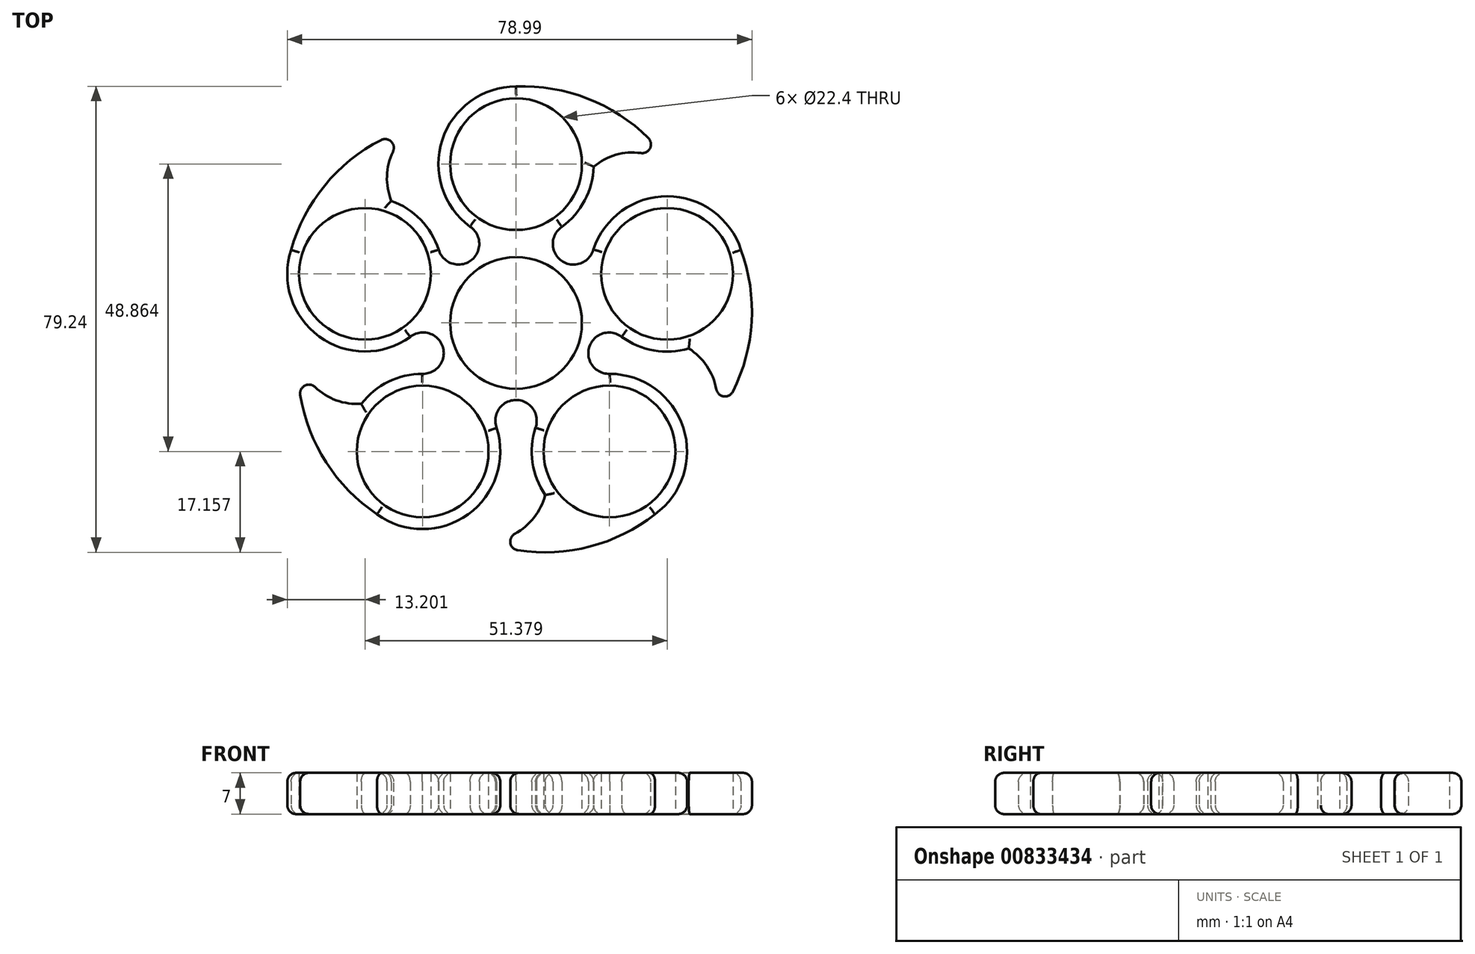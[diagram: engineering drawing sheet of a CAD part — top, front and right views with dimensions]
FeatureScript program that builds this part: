
annotation { "Feature Type Name" : "Feature", "Feature Type Description" : "" }
export const myFeature = defineFeature(function(context is Context, id is Id, definition is map)
    precondition{}
    {
        {
            var Q0;
            Q0=qCreatedBy(makeId("Top.planeOp"),FACE);
            var sketch = newSketch(context, id + "F0", { "sketchPlane" : qUnion([Q0])});
            skCircle(sketch, "E0", {"center": v(0, 0) * mm, "radius": 11.2 * mm});
            skArc(sketch, "E1", {"start": v(-12.76, -3.38) * mm, "mid": v(-12.55, -4.08) * mm, "end": v(-12.31, -4.76) * mm});
            skCircle(sketch, "E2", {"center": v(0, 27.01) * mm, "radius": 11.2 * mm});
            skArc(sketch, "E3", {"start": v(7.64, 16.25) * mm, "mid": v(11.63, 20.77) * mm, "end": v(13.2, 26.58) * mm});
            skCircle(sketch, "E4.1.0", {"center": v(-25.69, 8.35) * mm, "radius": 11.2 * mm});
            skArc(sketch, "E4.1.1", {"start": v(-13.1, 12.3) * mm, "mid": v(-16.16, 17.48) * mm, "end": v(-21.2, 20.76) * mm});
            skCircle(sketch, "E4.2.0", {"center": v(-15.88, -21.85) * mm, "radius": 11.2 * mm});
            skArc(sketch, "E4.2.1", {"start": v(-15.74, -8.65) * mm, "mid": v(-21.61, -9.96) * mm, "end": v(-26.3, -13.75) * mm});
            skCircle(sketch, "E4.3.0", {"center": v(15.88, -21.85) * mm, "radius": 11.2 * mm});
            skArc(sketch, "E4.3.1", {"start": v(23.64, -32.53) * mm, "mid": v(28.4, -17.69) * mm, "end": v(15.7, -8.65) * mm});
            skCircle(sketch, "E4.4.0", {"center": v(25.69, 8.35) * mm, "radius": 11.2 * mm});
            skArc(sketch, "E4.4.1", {"start": v(38.24, 12.43) * mm, "mid": v(25.6, 21.55) * mm, "end": v(13.08, 12.25) * mm});
            skArc(sketch, "E5", {"start": v(-13.15, 12.46) * mm, "mid": v(-7.69, 10.61) * mm, "end": v(-7.82, 16.38) * mm});
            skArc(sketch, "E6.1.0", {"start": v(-15.91, -8.65) * mm, "mid": v(-12.47, -4.03) * mm, "end": v(-18, -2.38) * mm});
            skArc(sketch, "E6.2.0", {"start": v(3.31, -17.8) * mm, "mid": v(-0.02, -13.1) * mm, "end": v(-3.3, -17.84) * mm});
            skArc(sketch, "E6.3.0", {"start": v(17.96, -2.35) * mm, "mid": v(12.46, -4.07) * mm, "end": v(15.95, -8.65) * mm});
            skArc(sketch, "E6.4.0", {"start": v(7.79, 16.35) * mm, "mid": v(7.72, 10.59) * mm, "end": v(13.16, 12.5) * mm});
            skArc(sketch, "E7", {"start": v(26.48, 26.58) * mm, "mid": v(15.03, 36.87) * mm, "end": v(0, 40.21) * mm});
            skArc(sketch, "E8", {"start": v(26.48, 26.58) * mm, "mid": v(19.84, 28.99) * mm, "end": v(13.2, 26.58) * mm});
            skArc(sketch, "E9.1.0", {"start": v(-17.1, 33.4) * mm, "mid": v(-30.42, 25.68) * mm, "end": v(-38.24, 12.43) * mm});
            skArc(sketch, "E9.1.1", {"start": v(-17.1, 33.4) * mm, "mid": v(-21.44, 27.82) * mm, "end": v(-21.2, 20.76) * mm});
            skArc(sketch, "E9.2.0", {"start": v(-37.05, -5.94) * mm, "mid": v(-33.83, -21) * mm, "end": v(-23.64, -32.53) * mm});
            skArc(sketch, "E9.2.1", {"start": v(-37.05, -5.94) * mm, "mid": v(-33.09, -11.8) * mm, "end": v(-26.3, -13.75) * mm});
            skArc(sketch, "E9.3.0", {"start": v(-5.8, -37.07) * mm, "mid": v(9.51, -38.66) * mm, "end": v(23.64, -32.53) * mm});
            skArc(sketch, "E9.3.1", {"start": v(-5.8, -37.07) * mm, "mid": v(1, -35.11) * mm, "end": v(4.95, -29.26) * mm});
            skArc(sketch, "E9.4.0", {"start": v(33.46, -16.97) * mm, "mid": v(39.7, -2.9) * mm, "end": v(38.24, 12.43) * mm});
            skArc(sketch, "E9.4.1", {"start": v(33.46, -16.97) * mm, "mid": v(33.7, -9.9) * mm, "end": v(29.36, -4.33) * mm});
            skArc(sketch, "E10.trimOffspring", {"start": v(-7.16, 11.09) * mm, "mid": v(-7.76, 10.68) * mm, "end": v(-8.33, 10.24) * mm});
            skArc(sketch, "E11.trimOffspring", {"start": v(8.33, 10.24) * mm, "mid": v(7.76, 10.68) * mm, "end": v(7.16, 11.09) * mm});
            skArc(sketch, "E12.trimOffspring", {"start": v(12.31, -4.76) * mm, "mid": v(12.55, -4.08) * mm, "end": v(12.76, -3.39) * mm});
            skArc(sketch, "E13.trimOffspring", {"start": v(-0.72, -13.18) * mm, "mid": v(0, -13.2) * mm, "end": v(0.72, -13.18) * mm});
            skArc(sketch, "E14.trimOffspring", {"start": v(-23.64, -32.53) * mm, "mid": v(-8.04, -32.48) * mm, "end": v(-3.38, -17.6) * mm});
            skArc(sketch, "E15.trimOffspring", {"start": v(3.37, -17.64) * mm, "mid": v(2.8, -23.64) * mm, "end": v(4.95, -29.26) * mm});
            skArc(sketch, "E16.trimOffspring", {"start": v(17.82, -2.25) * mm, "mid": v(23.34, -4.64) * mm, "end": v(29.36, -4.33) * mm});
            skArc(sketch, "E17.trimOffspring", {"start": v(0, 40.21) * mm, "mid": v(-12.58, 31) * mm, "end": v(-7.61, 16.23) * mm});
            skArc(sketch, "E18.trimOffspring", {"start": v(-38.24, 12.43) * mm, "mid": v(-33.37, -2.39) * mm, "end": v(-17.78, -2.22) * mm});
            skSolve(sketch);
        }
        {
            var Q0;
            Q0=makeQuery(id+"F0.imprint","IMPRINT",FACE,{"disambiguationData":[TD([[makeQuery(id+"F0.imprint","IMPRINT",EDGE,{"derivedFrom":sQuery(id+"F0.wireOp",EDGE,"E0")}),-1.0]])]});
            extrude(context, id + "F1", {"entities" : qUnion([Q0]), "depth" : 7 * mm, "offsetDistance" : 25 * mm});
        }
        {
            var Q0;
            Q0=makeQuery(id+"F1.opExtrude","CAP_EDGE",EDGE,{"disambiguationData":[OSD([sQuery(id+"F0.wireOp",EDGE,"E9.2.1")])],"isStart":false});
            var Q1;
            Q1=makeQuery(id+"F1.opExtrude","CAP_EDGE",EDGE,{"disambiguationData":[OSD([sQuery(id+"F0.wireOp",EDGE,"E9.2.0")])],"isStart":false});
            var Q2;
            Q2=makeQuery(id+"F1.opExtrude","CAP_EDGE",EDGE,{"disambiguationData":[OSD([sQuery(id+"F0.wireOp",EDGE,"E14.trimOffspring")])],"isStart":false});
            var Q3;
            Q3=makeQuery(id+"F1.opExtrude","CAP_EDGE",EDGE,{"disambiguationData":[OSD([sQuery(id+"F0.wireOp",EDGE,"E6.2.0")])],"isStart":false});
            var Q4;
            Q4=makeQuery(id+"F1.opExtrude","CAP_EDGE",EDGE,{"disambiguationData":[OSD([sQuery(id+"F0.wireOp",EDGE,"E15.trimOffspring")])],"isStart":false});
            var Q5;
            Q5=makeQuery(id+"F1.opExtrude","CAP_EDGE",EDGE,{"disambiguationData":[OSD([sQuery(id+"F0.wireOp",EDGE,"E9.3.1")])],"isStart":false});
            var Q6;
            Q6=makeQuery(id+"F1.opExtrude","CAP_EDGE",EDGE,{"disambiguationData":[OSD([sQuery(id+"F0.wireOp",EDGE,"E9.3.0")])],"isStart":false});
            var Q7;
            Q7=makeQuery(id+"F1.opExtrude","CAP_EDGE",EDGE,{"disambiguationData":[OSD([sQuery(id+"F0.wireOp",EDGE,"E4.3.1")])],"isStart":false});
            var Q8;
            Q8=makeQuery(id+"F1.opExtrude","CAP_EDGE",EDGE,{"disambiguationData":[OSD([sQuery(id+"F0.wireOp",EDGE,"E6.3.0")])],"isStart":false});
            var Q9;
            Q9=makeQuery(id+"F1.opExtrude","CAP_EDGE",EDGE,{"disambiguationData":[OSD([sQuery(id+"F0.wireOp",EDGE,"E16.trimOffspring")])],"isStart":false});
            var Q10;
            Q10=makeQuery(id+"F1.opExtrude","CAP_EDGE",EDGE,{"disambiguationData":[OSD([sQuery(id+"F0.wireOp",EDGE,"E9.4.1")])],"isStart":false});
            var Q11;
            Q11=makeQuery(id+"F1.opExtrude","CAP_EDGE",EDGE,{"disambiguationData":[OSD([sQuery(id+"F0.wireOp",EDGE,"E9.4.0")])],"isStart":false});
            var Q12;
            Q12=makeQuery(id+"F1.opExtrude","CAP_EDGE",EDGE,{"disambiguationData":[OSD([sQuery(id+"F0.wireOp",EDGE,"E4.4.1")])],"isStart":false});
            var Q13;
            Q13=makeQuery(id+"F1.opExtrude","CAP_EDGE",EDGE,{"disambiguationData":[OSD([sQuery(id+"F0.wireOp",EDGE,"E6.4.0")])],"isStart":false});
            var Q14;
            Q14=makeQuery(id+"F1.opExtrude","CAP_EDGE",EDGE,{"disambiguationData":[OSD([sQuery(id+"F0.wireOp",EDGE,"E3")])],"isStart":false});
            var Q15;
            Q15=makeQuery(id+"F1.opExtrude","CAP_EDGE",EDGE,{"disambiguationData":[OSD([sQuery(id+"F0.wireOp",EDGE,"E8")])],"isStart":false});
            var Q16;
            Q16=makeQuery(id+"F1.opExtrude","CAP_EDGE",EDGE,{"disambiguationData":[OSD([sQuery(id+"F0.wireOp",EDGE,"E7")])],"isStart":false});
            var Q17;
            Q17=makeQuery(id+"F1.opExtrude","CAP_EDGE",EDGE,{"disambiguationData":[OSD([sQuery(id+"F0.wireOp",EDGE,"E17.trimOffspring")])],"isStart":false});
            var Q18;
            Q18=makeQuery(id+"F1.opExtrude","CAP_EDGE",EDGE,{"disambiguationData":[OSD([sQuery(id+"F0.wireOp",EDGE,"E5")])],"isStart":false});
            var Q19;
            Q19=makeQuery(id+"F1.opExtrude","CAP_EDGE",EDGE,{"disambiguationData":[OSD([sQuery(id+"F0.wireOp",EDGE,"E4.1.1")])],"isStart":false});
            var Q20;
            Q20=makeQuery(id+"F1.opExtrude","CAP_EDGE",EDGE,{"disambiguationData":[OSD([sQuery(id+"F0.wireOp",EDGE,"E9.1.1")])],"isStart":false});
            var Q21;
            Q21=makeQuery(id+"F1.opExtrude","CAP_EDGE",EDGE,{"disambiguationData":[OSD([sQuery(id+"F0.wireOp",EDGE,"E9.1.0")])],"isStart":false});
            var Q22;
            Q22=makeQuery(id+"F1.opExtrude","CAP_EDGE",EDGE,{"disambiguationData":[OSD([sQuery(id+"F0.wireOp",EDGE,"E18.trimOffspring")])],"isStart":false});
            var Q23;
            Q23=makeQuery(id+"F1.opExtrude","CAP_EDGE",EDGE,{"disambiguationData":[OSD([sQuery(id+"F0.wireOp",EDGE,"E6.1.0")])],"isStart":false});
            var Q24;
            Q24=makeQuery(id+"F1.opExtrude","CAP_EDGE",EDGE,{"disambiguationData":[OSD([sQuery(id+"F0.wireOp",EDGE,"E4.2.1")])],"isStart":false});
            var Q25;
            Q25=makeQuery(id+"F1.opExtrude","SWEPT_EDGE",EDGE,{"disambiguationData":[OSD([sQuery(id+"F0.wireOp",EDGE,"E9.4.0"),sQuery(id+"F0.wireOp",EDGE,"E9.4.1")])]});
            var Q26;
            Q26=makeQuery(id+"F1.opExtrude","SWEPT_EDGE",EDGE,{"disambiguationData":[OSD([sQuery(id+"F0.wireOp",EDGE,"E9.3.0"),sQuery(id+"F0.wireOp",EDGE,"E9.3.1")])]});
            var Q27;
            Q27=makeQuery(id+"F1.opExtrude","SWEPT_EDGE",EDGE,{"disambiguationData":[OSD([sQuery(id+"F0.wireOp",EDGE,"E7"),sQuery(id+"F0.wireOp",EDGE,"E8")])]});
            var Q28;
            Q28=makeQuery(id+"F1.opExtrude","SWEPT_EDGE",EDGE,{"disambiguationData":[OSD([sQuery(id+"F0.wireOp",EDGE,"E9.1.0"),sQuery(id+"F0.wireOp",EDGE,"E9.1.1")])]});
            var Q29;
            Q29=makeQuery(id+"F1.opExtrude","SWEPT_EDGE",EDGE,{"disambiguationData":[OSD([sQuery(id+"F0.wireOp",EDGE,"E9.2.0"),sQuery(id+"F0.wireOp",EDGE,"E9.2.1")])]});
            fillet(context, id + "F2", {"entities" : qUnion([Q0, Q1, Q2, Q3, Q4, Q5, Q6, Q7, Q8, Q9, Q10, Q11, Q12, Q13, Q14, Q15, Q16, Q17, Q18, Q19, Q20, Q21, Q22, Q23, Q24, Q25, Q26, Q27, Q28, Q29]), "radius" : 1.5 * mm, "tangentPropagation" : true, "allowEdgeOverflow" : false});
        }
        {
            var Q0;
            {var subQ0=sQuery(id+"F0.wireOp",EDGE,"E9.1.1");var subQ1=sQuery(id+"F0.wireOp",EDGE,"E9.1.0");Q0=makeQuery(id+"F2.opFillet","BLEND_EDGE",EDGE,{"blendedFrom":[makeQuery(id+"F1.opExtrude","SWEPT_EDGE",EDGE,{"disambiguationData":[OSD([subQ1,subQ0])]}),makeQuery(id+"F1.opExtrude","CAP_FACE",FACE,{"disambiguationData":[OSD([sQuery(id+"F0.wireOp",EDGE,"E0"),sQuery(id+"F0.wireOp",EDGE,"E2"),sQuery(id+"F0.wireOp",EDGE,"E3"),sQuery(id+"F0.wireOp",EDGE,"E4.1.0"),sQuery(id+"F0.wireOp",EDGE,"E4.1.1"),sQuery(id+"F0.wireOp",EDGE,"E4.2.0"),sQuery(id+"F0.wireOp",EDGE,"E4.2.1"),sQuery(id+"F0.wireOp",EDGE,"E4.3.0"),sQuery(id+"F0.wireOp",EDGE,"E4.3.1"),sQuery(id+"F0.wireOp",EDGE,"E4.4.0"),sQuery(id+"F0.wireOp",EDGE,"E4.4.1"),sQuery(id+"F0.wireOp",EDGE,"E5"),sQuery(id+"F0.wireOp",EDGE,"E6.1.0"),sQuery(id+"F0.wireOp",EDGE,"E6.2.0"),sQuery(id+"F0.wireOp",EDGE,"E6.3.0"),sQuery(id+"F0.wireOp",EDGE,"E6.4.0"),sQuery(id+"F0.wireOp",EDGE,"E7"),sQuery(id+"F0.wireOp",EDGE,"E8"),subQ1,subQ0,sQuery(id+"F0.wireOp",EDGE,"E9.2.0"),sQuery(id+"F0.wireOp",EDGE,"E9.2.1"),sQuery(id+"F0.wireOp",EDGE,"E9.3.0"),sQuery(id+"F0.wireOp",EDGE,"E9.3.1"),sQuery(id+"F0.wireOp",EDGE,"E9.4.0"),sQuery(id+"F0.wireOp",EDGE,"E9.4.1"),sQuery(id+"F0.wireOp",EDGE,"E14.trimOffspring"),sQuery(id+"F0.wireOp",EDGE,"E15.trimOffspring"),sQuery(id+"F0.wireOp",EDGE,"E16.trimOffspring"),sQuery(id+"F0.wireOp",EDGE,"E17.trimOffspring"),sQuery(id+"F0.wireOp",EDGE,"E18.trimOffspring")])],"isStart":true})],"blendedInto":[makeQuery(id+"F1.opExtrude","CAP_FACE",FACE,{"disambiguationData":[OSD([sQuery(id+"F0.wireOp",EDGE,"E0"),sQuery(id+"F0.wireOp",EDGE,"E2"),sQuery(id+"F0.wireOp",EDGE,"E3"),sQuery(id+"F0.wireOp",EDGE,"E4.1.0"),sQuery(id+"F0.wireOp",EDGE,"E4.1.1"),sQuery(id+"F0.wireOp",EDGE,"E4.2.0"),sQuery(id+"F0.wireOp",EDGE,"E4.2.1"),sQuery(id+"F0.wireOp",EDGE,"E4.3.0"),sQuery(id+"F0.wireOp",EDGE,"E4.3.1"),sQuery(id+"F0.wireOp",EDGE,"E4.4.0"),sQuery(id+"F0.wireOp",EDGE,"E4.4.1"),sQuery(id+"F0.wireOp",EDGE,"E5"),sQuery(id+"F0.wireOp",EDGE,"E6.1.0"),sQuery(id+"F0.wireOp",EDGE,"E6.2.0"),sQuery(id+"F0.wireOp",EDGE,"E6.3.0"),sQuery(id+"F0.wireOp",EDGE,"E6.4.0"),sQuery(id+"F0.wireOp",EDGE,"E7"),sQuery(id+"F0.wireOp",EDGE,"E8"),subQ1,subQ0,sQuery(id+"F0.wireOp",EDGE,"E9.2.0"),sQuery(id+"F0.wireOp",EDGE,"E9.2.1"),sQuery(id+"F0.wireOp",EDGE,"E9.3.0"),sQuery(id+"F0.wireOp",EDGE,"E9.3.1"),sQuery(id+"F0.wireOp",EDGE,"E9.4.0"),sQuery(id+"F0.wireOp",EDGE,"E9.4.1"),sQuery(id+"F0.wireOp",EDGE,"E14.trimOffspring"),sQuery(id+"F0.wireOp",EDGE,"E15.trimOffspring"),sQuery(id+"F0.wireOp",EDGE,"E16.trimOffspring"),sQuery(id+"F0.wireOp",EDGE,"E17.trimOffspring"),sQuery(id+"F0.wireOp",EDGE,"E18.trimOffspring")])],"isStart":true})]});}
            var Q1;
            Q1=makeQuery(id+"F1.opExtrude","CAP_EDGE",EDGE,{"disambiguationData":[OSD([sQuery(id+"F0.wireOp",EDGE,"E9.1.1")])],"isStart":true});
            var Q2;
            Q2=makeQuery(id+"F1.opExtrude","CAP_EDGE",EDGE,{"disambiguationData":[OSD([sQuery(id+"F0.wireOp",EDGE,"E9.1.0")])],"isStart":true});
            var Q3;
            Q3=makeQuery(id+"F1.opExtrude","CAP_EDGE",EDGE,{"disambiguationData":[OSD([sQuery(id+"F0.wireOp",EDGE,"E18.trimOffspring")])],"isStart":true});
            var Q4;
            Q4=makeQuery(id+"F1.opExtrude","CAP_EDGE",EDGE,{"disambiguationData":[OSD([sQuery(id+"F0.wireOp",EDGE,"E6.1.0")])],"isStart":true});
            var Q5;
            Q5=makeQuery(id+"F1.opExtrude","CAP_EDGE",EDGE,{"disambiguationData":[OSD([sQuery(id+"F0.wireOp",EDGE,"E4.2.1")])],"isStart":true});
            var Q6;
            Q6=makeQuery(id+"F1.opExtrude","CAP_EDGE",EDGE,{"disambiguationData":[OSD([sQuery(id+"F0.wireOp",EDGE,"E9.2.1")])],"isStart":true});
            var Q7;
            {var subQ0=sQuery(id+"F0.wireOp",EDGE,"E9.2.1");var subQ1=sQuery(id+"F0.wireOp",EDGE,"E9.2.0");Q7=makeQuery(id+"F2.opFillet","BLEND_EDGE",EDGE,{"blendedFrom":[makeQuery(id+"F1.opExtrude","SWEPT_EDGE",EDGE,{"disambiguationData":[OSD([subQ1,subQ0])]}),makeQuery(id+"F1.opExtrude","CAP_FACE",FACE,{"disambiguationData":[OSD([sQuery(id+"F0.wireOp",EDGE,"E0"),sQuery(id+"F0.wireOp",EDGE,"E2"),sQuery(id+"F0.wireOp",EDGE,"E3"),sQuery(id+"F0.wireOp",EDGE,"E4.1.0"),sQuery(id+"F0.wireOp",EDGE,"E4.1.1"),sQuery(id+"F0.wireOp",EDGE,"E4.2.0"),sQuery(id+"F0.wireOp",EDGE,"E4.2.1"),sQuery(id+"F0.wireOp",EDGE,"E4.3.0"),sQuery(id+"F0.wireOp",EDGE,"E4.3.1"),sQuery(id+"F0.wireOp",EDGE,"E4.4.0"),sQuery(id+"F0.wireOp",EDGE,"E4.4.1"),sQuery(id+"F0.wireOp",EDGE,"E5"),sQuery(id+"F0.wireOp",EDGE,"E6.1.0"),sQuery(id+"F0.wireOp",EDGE,"E6.2.0"),sQuery(id+"F0.wireOp",EDGE,"E6.3.0"),sQuery(id+"F0.wireOp",EDGE,"E6.4.0"),sQuery(id+"F0.wireOp",EDGE,"E7"),sQuery(id+"F0.wireOp",EDGE,"E8"),sQuery(id+"F0.wireOp",EDGE,"E9.1.0"),sQuery(id+"F0.wireOp",EDGE,"E9.1.1"),subQ1,subQ0,sQuery(id+"F0.wireOp",EDGE,"E9.3.0"),sQuery(id+"F0.wireOp",EDGE,"E9.3.1"),sQuery(id+"F0.wireOp",EDGE,"E9.4.0"),sQuery(id+"F0.wireOp",EDGE,"E9.4.1"),sQuery(id+"F0.wireOp",EDGE,"E14.trimOffspring"),sQuery(id+"F0.wireOp",EDGE,"E15.trimOffspring"),sQuery(id+"F0.wireOp",EDGE,"E16.trimOffspring"),sQuery(id+"F0.wireOp",EDGE,"E17.trimOffspring"),sQuery(id+"F0.wireOp",EDGE,"E18.trimOffspring")])],"isStart":true})],"blendedInto":[makeQuery(id+"F1.opExtrude","CAP_FACE",FACE,{"disambiguationData":[OSD([sQuery(id+"F0.wireOp",EDGE,"E0"),sQuery(id+"F0.wireOp",EDGE,"E2"),sQuery(id+"F0.wireOp",EDGE,"E3"),sQuery(id+"F0.wireOp",EDGE,"E4.1.0"),sQuery(id+"F0.wireOp",EDGE,"E4.1.1"),sQuery(id+"F0.wireOp",EDGE,"E4.2.0"),sQuery(id+"F0.wireOp",EDGE,"E4.2.1"),sQuery(id+"F0.wireOp",EDGE,"E4.3.0"),sQuery(id+"F0.wireOp",EDGE,"E4.3.1"),sQuery(id+"F0.wireOp",EDGE,"E4.4.0"),sQuery(id+"F0.wireOp",EDGE,"E4.4.1"),sQuery(id+"F0.wireOp",EDGE,"E5"),sQuery(id+"F0.wireOp",EDGE,"E6.1.0"),sQuery(id+"F0.wireOp",EDGE,"E6.2.0"),sQuery(id+"F0.wireOp",EDGE,"E6.3.0"),sQuery(id+"F0.wireOp",EDGE,"E6.4.0"),sQuery(id+"F0.wireOp",EDGE,"E7"),sQuery(id+"F0.wireOp",EDGE,"E8"),sQuery(id+"F0.wireOp",EDGE,"E9.1.0"),sQuery(id+"F0.wireOp",EDGE,"E9.1.1"),subQ1,subQ0,sQuery(id+"F0.wireOp",EDGE,"E9.3.0"),sQuery(id+"F0.wireOp",EDGE,"E9.3.1"),sQuery(id+"F0.wireOp",EDGE,"E9.4.0"),sQuery(id+"F0.wireOp",EDGE,"E9.4.1"),sQuery(id+"F0.wireOp",EDGE,"E14.trimOffspring"),sQuery(id+"F0.wireOp",EDGE,"E15.trimOffspring"),sQuery(id+"F0.wireOp",EDGE,"E16.trimOffspring"),sQuery(id+"F0.wireOp",EDGE,"E17.trimOffspring"),sQuery(id+"F0.wireOp",EDGE,"E18.trimOffspring")])],"isStart":true})]});}
            var Q8;
            Q8=makeQuery(id+"F1.opExtrude","CAP_EDGE",EDGE,{"disambiguationData":[OSD([sQuery(id+"F0.wireOp",EDGE,"E9.2.0")])],"isStart":true});
            var Q9;
            Q9=makeQuery(id+"F1.opExtrude","CAP_EDGE",EDGE,{"disambiguationData":[OSD([sQuery(id+"F0.wireOp",EDGE,"E14.trimOffspring")])],"isStart":true});
            var Q10;
            Q10=makeQuery(id+"F1.opExtrude","CAP_EDGE",EDGE,{"disambiguationData":[OSD([sQuery(id+"F0.wireOp",EDGE,"E6.2.0")])],"isStart":true});
            var Q11;
            Q11=makeQuery(id+"F1.opExtrude","CAP_EDGE",EDGE,{"disambiguationData":[OSD([sQuery(id+"F0.wireOp",EDGE,"E15.trimOffspring")])],"isStart":true});
            var Q12;
            Q12=makeQuery(id+"F1.opExtrude","CAP_EDGE",EDGE,{"disambiguationData":[OSD([sQuery(id+"F0.wireOp",EDGE,"E9.3.1")])],"isStart":true});
            var Q13;
            {var subQ0=sQuery(id+"F0.wireOp",EDGE,"E9.3.1");var subQ1=sQuery(id+"F0.wireOp",EDGE,"E9.3.0");Q13=makeQuery(id+"F2.opFillet","BLEND_EDGE",EDGE,{"blendedFrom":[makeQuery(id+"F1.opExtrude","SWEPT_EDGE",EDGE,{"disambiguationData":[OSD([subQ1,subQ0])]}),makeQuery(id+"F1.opExtrude","CAP_FACE",FACE,{"disambiguationData":[OSD([sQuery(id+"F0.wireOp",EDGE,"E0"),sQuery(id+"F0.wireOp",EDGE,"E2"),sQuery(id+"F0.wireOp",EDGE,"E3"),sQuery(id+"F0.wireOp",EDGE,"E4.1.0"),sQuery(id+"F0.wireOp",EDGE,"E4.1.1"),sQuery(id+"F0.wireOp",EDGE,"E4.2.0"),sQuery(id+"F0.wireOp",EDGE,"E4.2.1"),sQuery(id+"F0.wireOp",EDGE,"E4.3.0"),sQuery(id+"F0.wireOp",EDGE,"E4.3.1"),sQuery(id+"F0.wireOp",EDGE,"E4.4.0"),sQuery(id+"F0.wireOp",EDGE,"E4.4.1"),sQuery(id+"F0.wireOp",EDGE,"E5"),sQuery(id+"F0.wireOp",EDGE,"E6.1.0"),sQuery(id+"F0.wireOp",EDGE,"E6.2.0"),sQuery(id+"F0.wireOp",EDGE,"E6.3.0"),sQuery(id+"F0.wireOp",EDGE,"E6.4.0"),sQuery(id+"F0.wireOp",EDGE,"E7"),sQuery(id+"F0.wireOp",EDGE,"E8"),sQuery(id+"F0.wireOp",EDGE,"E9.1.0"),sQuery(id+"F0.wireOp",EDGE,"E9.1.1"),sQuery(id+"F0.wireOp",EDGE,"E9.2.0"),sQuery(id+"F0.wireOp",EDGE,"E9.2.1"),subQ1,subQ0,sQuery(id+"F0.wireOp",EDGE,"E9.4.0"),sQuery(id+"F0.wireOp",EDGE,"E9.4.1"),sQuery(id+"F0.wireOp",EDGE,"E14.trimOffspring"),sQuery(id+"F0.wireOp",EDGE,"E15.trimOffspring"),sQuery(id+"F0.wireOp",EDGE,"E16.trimOffspring"),sQuery(id+"F0.wireOp",EDGE,"E17.trimOffspring"),sQuery(id+"F0.wireOp",EDGE,"E18.trimOffspring")])],"isStart":true})],"blendedInto":[makeQuery(id+"F1.opExtrude","CAP_FACE",FACE,{"disambiguationData":[OSD([sQuery(id+"F0.wireOp",EDGE,"E0"),sQuery(id+"F0.wireOp",EDGE,"E2"),sQuery(id+"F0.wireOp",EDGE,"E3"),sQuery(id+"F0.wireOp",EDGE,"E4.1.0"),sQuery(id+"F0.wireOp",EDGE,"E4.1.1"),sQuery(id+"F0.wireOp",EDGE,"E4.2.0"),sQuery(id+"F0.wireOp",EDGE,"E4.2.1"),sQuery(id+"F0.wireOp",EDGE,"E4.3.0"),sQuery(id+"F0.wireOp",EDGE,"E4.3.1"),sQuery(id+"F0.wireOp",EDGE,"E4.4.0"),sQuery(id+"F0.wireOp",EDGE,"E4.4.1"),sQuery(id+"F0.wireOp",EDGE,"E5"),sQuery(id+"F0.wireOp",EDGE,"E6.1.0"),sQuery(id+"F0.wireOp",EDGE,"E6.2.0"),sQuery(id+"F0.wireOp",EDGE,"E6.3.0"),sQuery(id+"F0.wireOp",EDGE,"E6.4.0"),sQuery(id+"F0.wireOp",EDGE,"E7"),sQuery(id+"F0.wireOp",EDGE,"E8"),sQuery(id+"F0.wireOp",EDGE,"E9.1.0"),sQuery(id+"F0.wireOp",EDGE,"E9.1.1"),sQuery(id+"F0.wireOp",EDGE,"E9.2.0"),sQuery(id+"F0.wireOp",EDGE,"E9.2.1"),subQ1,subQ0,sQuery(id+"F0.wireOp",EDGE,"E9.4.0"),sQuery(id+"F0.wireOp",EDGE,"E9.4.1"),sQuery(id+"F0.wireOp",EDGE,"E14.trimOffspring"),sQuery(id+"F0.wireOp",EDGE,"E15.trimOffspring"),sQuery(id+"F0.wireOp",EDGE,"E16.trimOffspring"),sQuery(id+"F0.wireOp",EDGE,"E17.trimOffspring"),sQuery(id+"F0.wireOp",EDGE,"E18.trimOffspring")])],"isStart":true})]});}
            var Q14;
            Q14=makeQuery(id+"F1.opExtrude","CAP_EDGE",EDGE,{"disambiguationData":[OSD([sQuery(id+"F0.wireOp",EDGE,"E9.3.0")])],"isStart":true});
            var Q15;
            Q15=makeQuery(id+"F1.opExtrude","CAP_EDGE",EDGE,{"disambiguationData":[OSD([sQuery(id+"F0.wireOp",EDGE,"E4.3.1")])],"isStart":true});
            var Q16;
            Q16=makeQuery(id+"F1.opExtrude","CAP_EDGE",EDGE,{"disambiguationData":[OSD([sQuery(id+"F0.wireOp",EDGE,"E6.3.0")])],"isStart":true});
            var Q17;
            Q17=makeQuery(id+"F1.opExtrude","CAP_EDGE",EDGE,{"disambiguationData":[OSD([sQuery(id+"F0.wireOp",EDGE,"E16.trimOffspring")])],"isStart":true});
            var Q18;
            Q18=makeQuery(id+"F1.opExtrude","CAP_EDGE",EDGE,{"disambiguationData":[OSD([sQuery(id+"F0.wireOp",EDGE,"E9.4.1")])],"isStart":true});
            var Q19;
            Q19=makeQuery(id+"F1.opExtrude","CAP_EDGE",EDGE,{"disambiguationData":[OSD([sQuery(id+"F0.wireOp",EDGE,"E9.4.0")])],"isStart":true});
            var Q20;
            {var subQ0=sQuery(id+"F0.wireOp",EDGE,"E9.4.1");var subQ1=sQuery(id+"F0.wireOp",EDGE,"E9.4.0");Q20=makeQuery(id+"F2.opFillet","BLEND_EDGE",EDGE,{"blendedFrom":[makeQuery(id+"F1.opExtrude","SWEPT_EDGE",EDGE,{"disambiguationData":[OSD([subQ1,subQ0])]}),makeQuery(id+"F1.opExtrude","CAP_FACE",FACE,{"disambiguationData":[OSD([sQuery(id+"F0.wireOp",EDGE,"E0"),sQuery(id+"F0.wireOp",EDGE,"E2"),sQuery(id+"F0.wireOp",EDGE,"E3"),sQuery(id+"F0.wireOp",EDGE,"E4.1.0"),sQuery(id+"F0.wireOp",EDGE,"E4.1.1"),sQuery(id+"F0.wireOp",EDGE,"E4.2.0"),sQuery(id+"F0.wireOp",EDGE,"E4.2.1"),sQuery(id+"F0.wireOp",EDGE,"E4.3.0"),sQuery(id+"F0.wireOp",EDGE,"E4.3.1"),sQuery(id+"F0.wireOp",EDGE,"E4.4.0"),sQuery(id+"F0.wireOp",EDGE,"E4.4.1"),sQuery(id+"F0.wireOp",EDGE,"E5"),sQuery(id+"F0.wireOp",EDGE,"E6.1.0"),sQuery(id+"F0.wireOp",EDGE,"E6.2.0"),sQuery(id+"F0.wireOp",EDGE,"E6.3.0"),sQuery(id+"F0.wireOp",EDGE,"E6.4.0"),sQuery(id+"F0.wireOp",EDGE,"E7"),sQuery(id+"F0.wireOp",EDGE,"E8"),sQuery(id+"F0.wireOp",EDGE,"E9.1.0"),sQuery(id+"F0.wireOp",EDGE,"E9.1.1"),sQuery(id+"F0.wireOp",EDGE,"E9.2.0"),sQuery(id+"F0.wireOp",EDGE,"E9.2.1"),sQuery(id+"F0.wireOp",EDGE,"E9.3.0"),sQuery(id+"F0.wireOp",EDGE,"E9.3.1"),subQ1,subQ0,sQuery(id+"F0.wireOp",EDGE,"E14.trimOffspring"),sQuery(id+"F0.wireOp",EDGE,"E15.trimOffspring"),sQuery(id+"F0.wireOp",EDGE,"E16.trimOffspring"),sQuery(id+"F0.wireOp",EDGE,"E17.trimOffspring"),sQuery(id+"F0.wireOp",EDGE,"E18.trimOffspring")])],"isStart":true})],"blendedInto":[makeQuery(id+"F1.opExtrude","CAP_FACE",FACE,{"disambiguationData":[OSD([sQuery(id+"F0.wireOp",EDGE,"E0"),sQuery(id+"F0.wireOp",EDGE,"E2"),sQuery(id+"F0.wireOp",EDGE,"E3"),sQuery(id+"F0.wireOp",EDGE,"E4.1.0"),sQuery(id+"F0.wireOp",EDGE,"E4.1.1"),sQuery(id+"F0.wireOp",EDGE,"E4.2.0"),sQuery(id+"F0.wireOp",EDGE,"E4.2.1"),sQuery(id+"F0.wireOp",EDGE,"E4.3.0"),sQuery(id+"F0.wireOp",EDGE,"E4.3.1"),sQuery(id+"F0.wireOp",EDGE,"E4.4.0"),sQuery(id+"F0.wireOp",EDGE,"E4.4.1"),sQuery(id+"F0.wireOp",EDGE,"E5"),sQuery(id+"F0.wireOp",EDGE,"E6.1.0"),sQuery(id+"F0.wireOp",EDGE,"E6.2.0"),sQuery(id+"F0.wireOp",EDGE,"E6.3.0"),sQuery(id+"F0.wireOp",EDGE,"E6.4.0"),sQuery(id+"F0.wireOp",EDGE,"E7"),sQuery(id+"F0.wireOp",EDGE,"E8"),sQuery(id+"F0.wireOp",EDGE,"E9.1.0"),sQuery(id+"F0.wireOp",EDGE,"E9.1.1"),sQuery(id+"F0.wireOp",EDGE,"E9.2.0"),sQuery(id+"F0.wireOp",EDGE,"E9.2.1"),sQuery(id+"F0.wireOp",EDGE,"E9.3.0"),sQuery(id+"F0.wireOp",EDGE,"E9.3.1"),subQ1,subQ0,sQuery(id+"F0.wireOp",EDGE,"E14.trimOffspring"),sQuery(id+"F0.wireOp",EDGE,"E15.trimOffspring"),sQuery(id+"F0.wireOp",EDGE,"E16.trimOffspring"),sQuery(id+"F0.wireOp",EDGE,"E17.trimOffspring"),sQuery(id+"F0.wireOp",EDGE,"E18.trimOffspring")])],"isStart":true})]});}
            var Q21;
            Q21=makeQuery(id+"F1.opExtrude","CAP_EDGE",EDGE,{"disambiguationData":[OSD([sQuery(id+"F0.wireOp",EDGE,"E4.4.1")])],"isStart":true});
            var Q22;
            Q22=makeQuery(id+"F1.opExtrude","CAP_EDGE",EDGE,{"disambiguationData":[OSD([sQuery(id+"F0.wireOp",EDGE,"E6.4.0")])],"isStart":true});
            var Q23;
            Q23=makeQuery(id+"F1.opExtrude","CAP_EDGE",EDGE,{"disambiguationData":[OSD([sQuery(id+"F0.wireOp",EDGE,"E3")])],"isStart":true});
            var Q24;
            {var subQ0=sQuery(id+"F0.wireOp",EDGE,"E8");var subQ1=sQuery(id+"F0.wireOp",EDGE,"E7");Q24=makeQuery(id+"F2.opFillet","BLEND_EDGE",EDGE,{"blendedFrom":[makeQuery(id+"F1.opExtrude","SWEPT_EDGE",EDGE,{"disambiguationData":[OSD([subQ1,subQ0])]}),makeQuery(id+"F1.opExtrude","CAP_FACE",FACE,{"disambiguationData":[OSD([sQuery(id+"F0.wireOp",EDGE,"E0"),sQuery(id+"F0.wireOp",EDGE,"E2"),sQuery(id+"F0.wireOp",EDGE,"E3"),sQuery(id+"F0.wireOp",EDGE,"E4.1.0"),sQuery(id+"F0.wireOp",EDGE,"E4.1.1"),sQuery(id+"F0.wireOp",EDGE,"E4.2.0"),sQuery(id+"F0.wireOp",EDGE,"E4.2.1"),sQuery(id+"F0.wireOp",EDGE,"E4.3.0"),sQuery(id+"F0.wireOp",EDGE,"E4.3.1"),sQuery(id+"F0.wireOp",EDGE,"E4.4.0"),sQuery(id+"F0.wireOp",EDGE,"E4.4.1"),sQuery(id+"F0.wireOp",EDGE,"E5"),sQuery(id+"F0.wireOp",EDGE,"E6.1.0"),sQuery(id+"F0.wireOp",EDGE,"E6.2.0"),sQuery(id+"F0.wireOp",EDGE,"E6.3.0"),sQuery(id+"F0.wireOp",EDGE,"E6.4.0"),subQ1,subQ0,sQuery(id+"F0.wireOp",EDGE,"E9.1.0"),sQuery(id+"F0.wireOp",EDGE,"E9.1.1"),sQuery(id+"F0.wireOp",EDGE,"E9.2.0"),sQuery(id+"F0.wireOp",EDGE,"E9.2.1"),sQuery(id+"F0.wireOp",EDGE,"E9.3.0"),sQuery(id+"F0.wireOp",EDGE,"E9.3.1"),sQuery(id+"F0.wireOp",EDGE,"E9.4.0"),sQuery(id+"F0.wireOp",EDGE,"E9.4.1"),sQuery(id+"F0.wireOp",EDGE,"E14.trimOffspring"),sQuery(id+"F0.wireOp",EDGE,"E15.trimOffspring"),sQuery(id+"F0.wireOp",EDGE,"E16.trimOffspring"),sQuery(id+"F0.wireOp",EDGE,"E17.trimOffspring"),sQuery(id+"F0.wireOp",EDGE,"E18.trimOffspring")])],"isStart":true})],"blendedInto":[makeQuery(id+"F1.opExtrude","CAP_FACE",FACE,{"disambiguationData":[OSD([sQuery(id+"F0.wireOp",EDGE,"E0"),sQuery(id+"F0.wireOp",EDGE,"E2"),sQuery(id+"F0.wireOp",EDGE,"E3"),sQuery(id+"F0.wireOp",EDGE,"E4.1.0"),sQuery(id+"F0.wireOp",EDGE,"E4.1.1"),sQuery(id+"F0.wireOp",EDGE,"E4.2.0"),sQuery(id+"F0.wireOp",EDGE,"E4.2.1"),sQuery(id+"F0.wireOp",EDGE,"E4.3.0"),sQuery(id+"F0.wireOp",EDGE,"E4.3.1"),sQuery(id+"F0.wireOp",EDGE,"E4.4.0"),sQuery(id+"F0.wireOp",EDGE,"E4.4.1"),sQuery(id+"F0.wireOp",EDGE,"E5"),sQuery(id+"F0.wireOp",EDGE,"E6.1.0"),sQuery(id+"F0.wireOp",EDGE,"E6.2.0"),sQuery(id+"F0.wireOp",EDGE,"E6.3.0"),sQuery(id+"F0.wireOp",EDGE,"E6.4.0"),subQ1,subQ0,sQuery(id+"F0.wireOp",EDGE,"E9.1.0"),sQuery(id+"F0.wireOp",EDGE,"E9.1.1"),sQuery(id+"F0.wireOp",EDGE,"E9.2.0"),sQuery(id+"F0.wireOp",EDGE,"E9.2.1"),sQuery(id+"F0.wireOp",EDGE,"E9.3.0"),sQuery(id+"F0.wireOp",EDGE,"E9.3.1"),sQuery(id+"F0.wireOp",EDGE,"E9.4.0"),sQuery(id+"F0.wireOp",EDGE,"E9.4.1"),sQuery(id+"F0.wireOp",EDGE,"E14.trimOffspring"),sQuery(id+"F0.wireOp",EDGE,"E15.trimOffspring"),sQuery(id+"F0.wireOp",EDGE,"E16.trimOffspring"),sQuery(id+"F0.wireOp",EDGE,"E17.trimOffspring"),sQuery(id+"F0.wireOp",EDGE,"E18.trimOffspring")])],"isStart":true})]});}
            var Q25;
            Q25=makeQuery(id+"F1.opExtrude","CAP_EDGE",EDGE,{"disambiguationData":[OSD([sQuery(id+"F0.wireOp",EDGE,"E7")])],"isStart":true});
            var Q26;
            Q26=makeQuery(id+"F1.opExtrude","CAP_EDGE",EDGE,{"disambiguationData":[OSD([sQuery(id+"F0.wireOp",EDGE,"E8")])],"isStart":true});
            var Q27;
            Q27=makeQuery(id+"F1.opExtrude","CAP_EDGE",EDGE,{"disambiguationData":[OSD([sQuery(id+"F0.wireOp",EDGE,"E17.trimOffspring")])],"isStart":true});
            var Q28;
            Q28=makeQuery(id+"F1.opExtrude","CAP_EDGE",EDGE,{"disambiguationData":[OSD([sQuery(id+"F0.wireOp",EDGE,"E5")])],"isStart":true});
            var Q29;
            Q29=makeQuery(id+"F1.opExtrude","CAP_EDGE",EDGE,{"disambiguationData":[OSD([sQuery(id+"F0.wireOp",EDGE,"E4.1.1")])],"isStart":true});
            fillet(context, id + "F3", {"entities" : qUnion([Q0, Q1, Q2, Q3, Q4, Q5, Q6, Q7, Q8, Q9, Q10, Q11, Q12, Q13, Q14, Q15, Q16, Q17, Q18, Q19, Q20, Q21, Q22, Q23, Q24, Q25, Q26, Q27, Q28, Q29]), "radius" : 1.5 * mm, "tangentPropagation" : true, "allowEdgeOverflow" : false});
        }
    });
